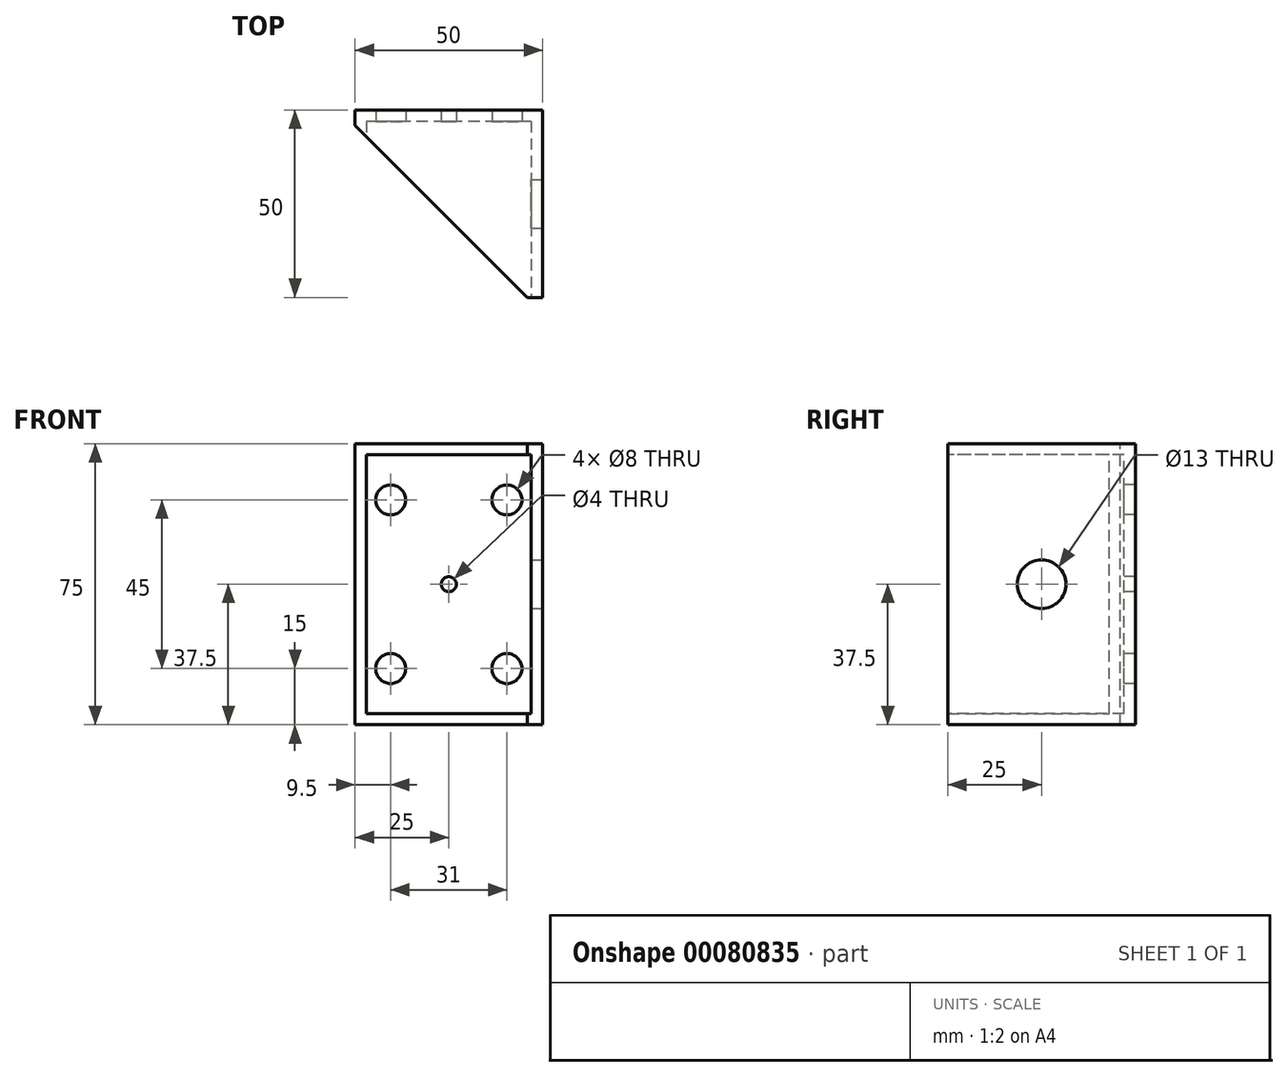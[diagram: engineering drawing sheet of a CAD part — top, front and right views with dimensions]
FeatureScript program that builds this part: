
annotation { "Feature Type Name" : "Feature", "Feature Type Description" : "" }
export const myFeature = defineFeature(function(context is Context, id is Id, definition is map)
    precondition{}
    {
        {
            var Q0;
            Q0=qCreatedBy(makeId("Front.planeOp"),FACE);
            var sketch = newSketch(context, id + "F0", { "sketchPlane" : qUnion([Q0])});
            skLineSegment(sketch, "E0.bottom", {"start": v(25, -37.5) * mm, "end": v(-25, -37.5) * mm});
            skLineSegment(sketch, "E0.top", {"start": v(25, 37.5) * mm, "end": v(-25, 37.5) * mm});
            skLineSegment(sketch, "E0.left", {"start": v(25, -37.5) * mm, "end": v(25, 37.5) * mm});
            skLineSegment(sketch, "E0.right", {"start": v(-25, -37.5) * mm, "end": v(-25, 37.5) * mm});
            skPoint(sketch, "E0.middle", {"position": v(0, 0) * mm});
            skSolve(sketch);
        }
        {
            var Q0;
            Q0=makeQuery(id+"F0.imprint","IMPRINT",FACE,{"disambiguationData":[TD([[makeQuery(id+"F0.imprint","IMPRINT",EDGE,{"derivedFrom":sQuery(id+"F0.wireOp",EDGE,"E0.bottom")}),-1.0]])]});
            extrude(context, id + "F1", {"entities" : qUnion([Q0]), "depth" : 50 * mm});
        }
        {
            var Q0;
            Q0=makeQuery(id+"F1.opExtrude","CAP_FACE",FACE,{"disambiguationData":[OSD([sQuery(id+"F0.wireOp",EDGE,"E0.bottom"),sQuery(id+"F0.wireOp",EDGE,"E0.top"),sQuery(id+"F0.wireOp",EDGE,"E0.left"),sQuery(id+"F0.wireOp",EDGE,"E0.right")])],"isStart":false});
            var sketch = newSketch(context, id + "F2", { "sketchPlane" : qUnion([Q0])});
            skLineSegment(sketch, "E1.bottom", {"start": v(22, -34.5) * mm, "end": v(-22, -34.5) * mm});
            skLineSegment(sketch, "E1.top", {"start": v(22, 34.5) * mm, "end": v(-22, 34.5) * mm});
            skLineSegment(sketch, "E1.left", {"start": v(22, -34.5) * mm, "end": v(22, 34.5) * mm});
            skLineSegment(sketch, "E1.right", {"start": v(-22, -34.5) * mm, "end": v(-22, 34.5) * mm});
            skPoint(sketch, "E1.middle", {"position": v(0, 0) * mm});
            skSolve(sketch);
        }
        {
            var Q0;
            Q0=makeQuery(id+"F2.imprint","IMPRINT",FACE,{"disambiguationData":[TD([[makeQuery(id+"F2.imprint","IMPRINT",EDGE,{"derivedFrom":sQuery(id+"F2.wireOp",EDGE,"E1.bottom")}),-1.0]])]});
            extrude(context, id + "F3", {"entities" : qUnion([Q0]), "operationType" : NewBodyOperationType.REMOVE, "oppositeDirection" : true, "depth" : 47 * mm});
        }
        {
            var Q0;
            Q0=makeQuery(id+"F1.opExtrude","CAP_EDGE",EDGE,{"disambiguationData":[OSD([sQuery(id+"F0.wireOp",EDGE,"E0.right")])],"isStart":false});
            chamfer(context, id + "F4", {"entities" : qUnion([Q0]), "width" : 46 * mm, "tangentPropagation" : true});
        }
        {
            var Q0;
            Q0=makeQuery(id+"F3.boolean.opBoolean","COPY",FACE,{"derivedFrom":makeQuery(id+"F3.opExtrude","CAP_FACE",FACE,{"disambiguationData":[OSD([sQuery(id+"F2.wireOp",EDGE,"E1.bottom"),sQuery(id+"F2.wireOp",EDGE,"E1.top"),sQuery(id+"F2.wireOp",EDGE,"E1.left"),sQuery(id+"F2.wireOp",EDGE,"E1.right")])],"isStart":false})});
            var sketch = newSketch(context, id + "F5", { "sketchPlane" : qUnion([Q0])});
            skLineSegment(sketch, "E2.bottom", {"start": v(15.5, -22.5) * mm, "end": v(-15.5, -22.5) * mm, "construction": true});
            skLineSegment(sketch, "E2.top", {"start": v(15.5, 22.5) * mm, "end": v(-15.5, 22.5) * mm, "construction": true});
            skLineSegment(sketch, "E2.left", {"start": v(15.5, -22.5) * mm, "end": v(15.5, 22.5) * mm, "construction": true});
            skLineSegment(sketch, "E2.right", {"start": v(-15.5, -22.5) * mm, "end": v(-15.5, 22.5) * mm, "construction": true});
            skPoint(sketch, "E2.middle", {"position": v(0, 0) * mm});
            skCircle(sketch, "E3", {"center": v(-15.5, 22.5) * mm, "radius": 4 * mm});
            skCircle(sketch, "E4", {"center": v(15.5, 22.5) * mm, "radius": 4 * mm});
            skCircle(sketch, "E5", {"center": v(-15.5, -22.5) * mm, "radius": 4 * mm});
            skCircle(sketch, "E6", {"center": v(15.5, -22.5) * mm, "radius": 4 * mm});
            skCircle(sketch, "E7", {"center": v(0, 0) * mm, "radius": 2 * mm});
            skSolve(sketch);
        }
        {
            var Q0;
            Q0=makeQuery(id+"F5.imprint","IMPRINT",FACE,{"disambiguationData":[TD([[makeQuery(id+"F5.imprint","IMPRINT",EDGE,{"derivedFrom":sQuery(id+"F5.wireOp",EDGE,"E3")}),1.0]])]});
            var Q1;
            Q1=makeQuery(id+"F5.imprint","IMPRINT",FACE,{"disambiguationData":[TD([[makeQuery(id+"F5.imprint","IMPRINT",EDGE,{"derivedFrom":sQuery(id+"F5.wireOp",EDGE,"E4")}),1.0]])]});
            var Q2;
            Q2=makeQuery(id+"F5.imprint","IMPRINT",FACE,{"disambiguationData":[TD([[makeQuery(id+"F5.imprint","IMPRINT",EDGE,{"derivedFrom":sQuery(id+"F5.wireOp",EDGE,"E6")}),1.0]])]});
            var Q3;
            Q3=makeQuery(id+"F5.imprint","IMPRINT",FACE,{"disambiguationData":[TD([[makeQuery(id+"F5.imprint","IMPRINT",EDGE,{"derivedFrom":sQuery(id+"F5.wireOp",EDGE,"E5")}),1.0]])]});
            var Q4;
            Q4=makeQuery(id+"F5.imprint","IMPRINT",FACE,{"disambiguationData":[TD([[makeQuery(id+"F5.imprint","IMPRINT",EDGE,{"derivedFrom":sQuery(id+"F5.wireOp",EDGE,"E7")}),1.0]])]});
            extrude(context, id + "F6", {"entities" : qUnion([Q0, Q1, Q2, Q3, Q4]), "operationType" : NewBodyOperationType.REMOVE, "endBound" : BoundingType.UP_TO_NEXT, "oppositeDirection" : true, "depth" : 25 * mm});
        }
        {
            var Q0;
            Q0=makeQuery(id+"F1.opExtrude","SWEPT_FACE",FACE,{"disambiguationData":[OSD([sQuery(id+"F0.wireOp",EDGE,"E0.left")])]});
            var sketch = newSketch(context, id + "F7", { "sketchPlane" : qUnion([Q0])});
            skLineSegment(sketch, "E8", {"start": v(-25, 37.5) * mm, "end": v(-25, -37.5) * mm, "construction": true});
            skCircle(sketch, "E9", {"center": v(-25, 0) * mm, "radius": 6.5 * mm});
            skSolve(sketch);
        }
        {
            var Q0;
            Q0=makeQuery(id+"F7.imprint","IMPRINT",FACE,{"disambiguationData":[TD([[makeQuery(id+"F7.imprint","IMPRINT",EDGE,{"derivedFrom":sQuery(id+"F7.wireOp",EDGE,"E9")}),1.0]])]});
            extrude(context, id + "F8", {"entities" : qUnion([Q0]), "operationType" : NewBodyOperationType.REMOVE, "endBound" : BoundingType.UP_TO_NEXT, "oppositeDirection" : true, "depth" : 25 * mm});
        }
    });
